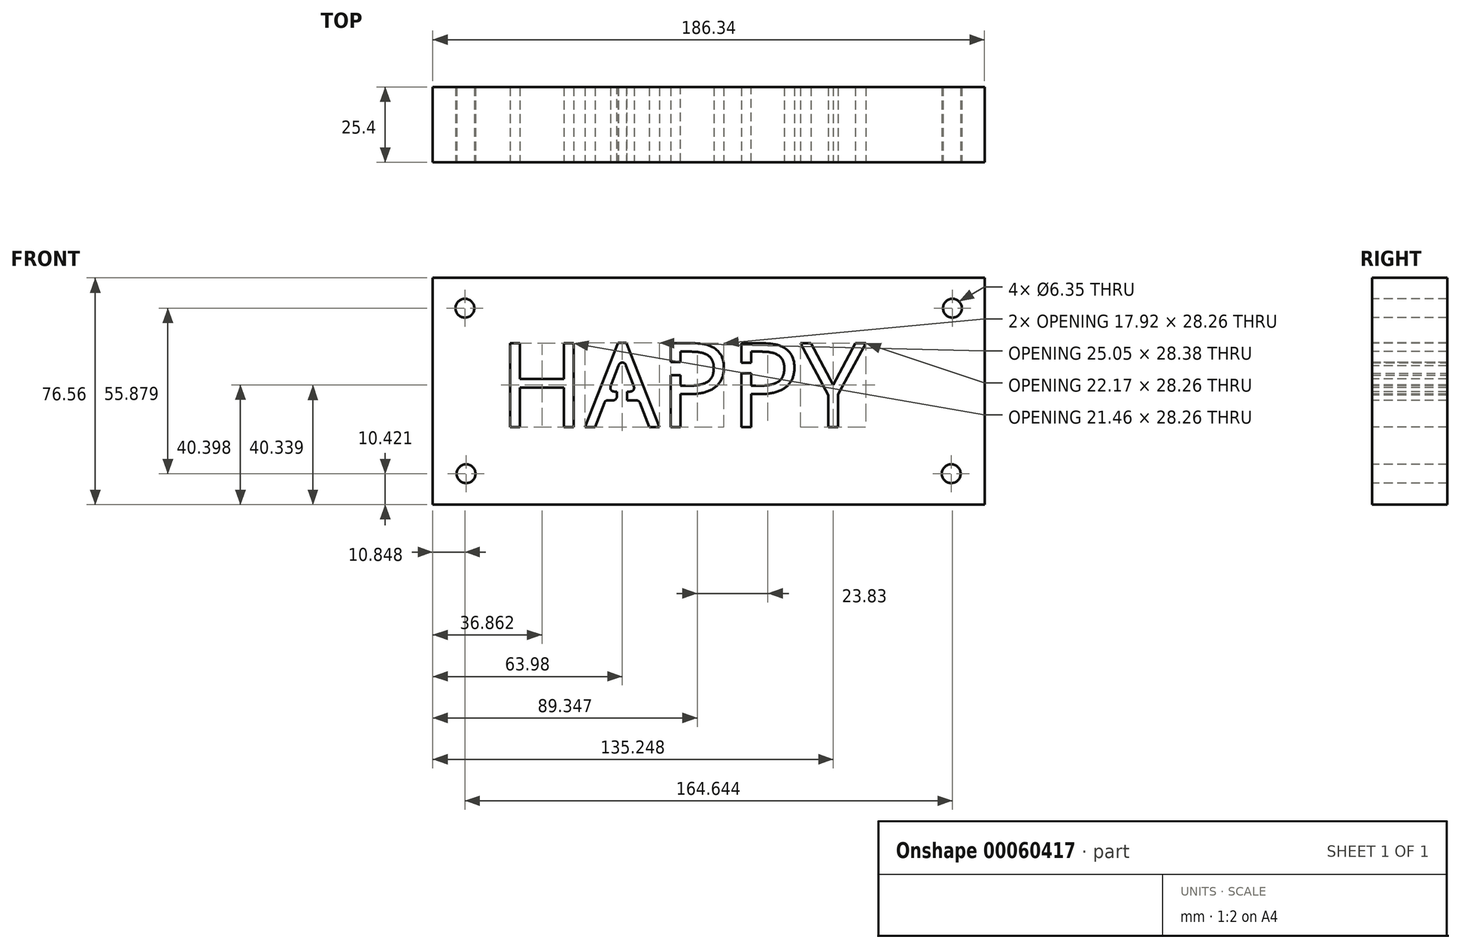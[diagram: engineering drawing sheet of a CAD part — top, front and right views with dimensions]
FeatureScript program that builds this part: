
annotation { "Feature Type Name" : "Feature", "Feature Type Description" : "" }
export const myFeature = defineFeature(function(context is Context, id is Id, definition is map)
    precondition{}
    {
        {
            var Q0;
            Q0=qCreatedBy(makeId("Front.planeOp"),FACE);
            var sketch = newSketch(context, id + "F0", { "sketchPlane" : qUnion([Q0])});
            skLineSegment(sketch, "E0.rect.bottom", {"start": v(93.17, 38.28) * mm, "end": v(-93.17, 38.28) * mm});
            skLineSegment(sketch, "E0.rect.top", {"start": v(93.17, -38.28) * mm, "end": v(-93.17, -38.28) * mm});
            skLineSegment(sketch, "E0.rect.left", {"start": v(93.17, 38.28) * mm, "end": v(93.17, -38.28) * mm});
            skLineSegment(sketch, "E0.rect.right", {"start": v(-93.17, 38.28) * mm, "end": v(-93.17, -38.28) * mm});
            skPoint(sketch, "E0.rect.middle", {"position": v(0, 0) * mm});
            skSolve(sketch);
        }
        {
            var Q0;
            Q0 = qSketchRegion(id + "F0", true);
            extrude(context, id + "F1", {"entities" : qUnion([Q0]), "depth" : 25.4 * mm});
        }
        {
            var Q0;
            Q0=makeQuery(id+"F1.opExtrude","CAP_FACE",FACE,{"disambiguationData":[OSD([sQuery(id+"F0.wireOp",EDGE,"E0.rect.bottom"),sQuery(id+"F0.wireOp",EDGE,"E0.rect.top"),sQuery(id+"F0.wireOp",EDGE,"E0.rect.left"),sQuery(id+"F0.wireOp",EDGE,"E0.rect.right")])],"isStart":false});
            var sketch = newSketch(context, id + "F2", { "sketchPlane" : qUnion([Q0])});
            skText(sketch, "E1", { "text": "HAPPY\n", "fontName": "OpenSans-Regular.ttf"});
            const initialGuessF2  = {"E1": [-0.07092, -0.01207, 1, 0, 0.0285]};
            skSetInitialGuess(sketch, initialGuessF2);
            skSolve(sketch);
        }
        {
            var Q0;
            Q0 = qSketchRegion(id + "F2", true);
            extrude(context, id + "F3", {"entities" : qUnion([Q0]), "operationType" : NewBodyOperationType.REMOVE, "oppositeDirection" : true, "depth" : 0.03 * mm});
        }
        {
            var Q0;
            {var subQ0=sQuery(id+"F0.wireOp",EDGE,"E0.rect.top");var subQ1=sQuery(id+"F0.wireOp",EDGE,"E0.rect.right");var subQ2=sQuery(id+"F0.wireOp",EDGE,"E0.rect.bottom");var subQ3=sQuery(id+"F0.wireOp",EDGE,"E0.rect.left");Q0=makeQuery(id+"F3.boolean.opBoolean","SPLIT",FACE,{"disambiguationData":[TD([makeQuery(id+"F1.opExtrude","SWEPT_FACE",FACE,{"disambiguationData":[OSD([subQ2])]})])],"derivedFrom":makeQuery(id+"F1.opExtrude","CAP_FACE",FACE,{"disambiguationData":[OSD([subQ2,subQ0,subQ3,subQ1])],"isStart":false})});}
            var sketch = newSketch(context, id + "F4", { "sketchPlane" : qUnion([Q0])});
            skLineSegment(sketch, "E2.rect.bottom", {"start": v(-27.48, 0) * mm, "end": v(-31, 0) * mm});
            skLineSegment(sketch, "E2.rect.top", {"start": v(-27.48, -6.16) * mm, "end": v(-31, -6.16) * mm});
            skLineSegment(sketch, "E2.rect.left", {"start": v(-27.48, 0) * mm, "end": v(-27.48, -6.16) * mm});
            skLineSegment(sketch, "E2.rect.right", {"start": v(-31, 0) * mm, "end": v(-31, -6.16) * mm});
            skPoint(sketch, "E2.rect.middle", {"position": v(-29.24, -3.08) * mm});
            skLineSegment(sketch, "E3.rect.bottom", {"start": v(-7.5, 5.36) * mm, "end": v(-18.04, 5.36) * mm});
            skLineSegment(sketch, "E3.rect.top", {"start": v(-7.5, 9.8) * mm, "end": v(-18.04, 9.8) * mm});
            skLineSegment(sketch, "E3.rect.left", {"start": v(-7.5, 5.36) * mm, "end": v(-7.5, 9.8) * mm});
            skLineSegment(sketch, "E3.rect.right", {"start": v(-18.04, 5.36) * mm, "end": v(-18.04, 9.8) * mm});
            skPoint(sketch, "E3.rect.middle", {"position": v(-12.77, 7.58) * mm});
            skLineSegment(sketch, "E4.rect.bottom", {"start": v(16.12, 5.98) * mm, "end": v(6, 5.98) * mm});
            skLineSegment(sketch, "E4.rect.top", {"start": v(16.12, 9.63) * mm, "end": v(6, 9.63) * mm});
            skLineSegment(sketch, "E4.rect.left", {"start": v(16.12, 5.98) * mm, "end": v(16.12, 9.63) * mm});
            skLineSegment(sketch, "E4.rect.right", {"start": v(6, 5.98) * mm, "end": v(6, 9.63) * mm});
            skPoint(sketch, "E4.rect.middle", {"position": v(11.06, 7.8) * mm});
            skSolve(sketch);
        }
        {
            var Q0;
            Q0 = qSketchRegion(id + "F4", true);
            extrude(context, id + "F5", {"entities" : qUnion([Q0]), "operationType" : NewBodyOperationType.ADD, "oppositeDirection" : true, "depth" : 5.08 * mm});
        }
        {
            var Q0;
            Q0=makeQuery(id+"F3.boolean.opBoolean","COPY",FACE,{"derivedFrom":makeQuery(id+"F3.opExtrude","CAP_FACE",FACE,{"disambiguationData":[OSD([sQuery(id+"F2.wireOp",EDGE,"E1.sketch_text.stroke-0"),sQuery(id+"F2.wireOp",EDGE,"E1.sketch_text.stroke-1"),sQuery(id+"F2.wireOp",EDGE,"E1.sketch_text.stroke-2"),sQuery(id+"F2.wireOp",EDGE,"E1.sketch_text.stroke-3"),sQuery(id+"F2.wireOp",EDGE,"E1.sketch_text.stroke-4"),sQuery(id+"F2.wireOp",EDGE,"E1.sketch_text.stroke-5"),sQuery(id+"F2.wireOp",EDGE,"E1.sketch_text.stroke-6"),sQuery(id+"F2.wireOp",EDGE,"E1.sketch_text.stroke-7"),sQuery(id+"F2.wireOp",EDGE,"E1.sketch_text.stroke-8"),sQuery(id+"F2.wireOp",EDGE,"E1.sketch_text.stroke-9"),sQuery(id+"F2.wireOp",EDGE,"E1.sketch_text.stroke-10"),sQuery(id+"F2.wireOp",EDGE,"E1.sketch_text.stroke-11")])],"isStart":false})});
            var Q1;
            Q1=makeQuery(id+"F3.boolean.opBoolean","COPY",FACE,{"derivedFrom":makeQuery(id+"F3.opExtrude","CAP_FACE",FACE,{"disambiguationData":[OSD([sQuery(id+"F2.wireOp",EDGE,"E1.sketch_text.stroke-12"),sQuery(id+"F2.wireOp",EDGE,"E1.sketch_text.stroke-13"),sQuery(id+"F2.wireOp",EDGE,"E1.sketch_text.stroke-14"),sQuery(id+"F2.wireOp",EDGE,"E1.sketch_text.stroke-15"),sQuery(id+"F2.wireOp",EDGE,"E1.sketch_text.stroke-16"),sQuery(id+"F2.wireOp",EDGE,"E1.sketch_text.stroke-17"),sQuery(id+"F2.wireOp",EDGE,"E1.sketch_text.stroke-18"),sQuery(id+"F2.wireOp",EDGE,"E1.sketch_text.stroke-19"),sQuery(id+"F2.wireOp",EDGE,"E1.sketch_text.stroke-20"),sQuery(id+"F2.wireOp",EDGE,"E1.sketch_text.stroke-21"),sQuery(id+"F2.wireOp",EDGE,"E1.sketch_text.stroke-22"),sQuery(id+"F2.wireOp",EDGE,"E1.sketch_text.stroke-23"),sQuery(id+"F2.wireOp",EDGE,"E1.sketch_text.stroke-24")])],"isStart":false})});
            var Q2;
            Q2=makeQuery(id+"F3.boolean.opBoolean","COPY",FACE,{"derivedFrom":makeQuery(id+"F3.opExtrude","CAP_FACE",FACE,{"disambiguationData":[OSD([sQuery(id+"F2.wireOp",EDGE,"E1.sketch_text.stroke-25"),sQuery(id+"F2.wireOp",EDGE,"E1.sketch_text.stroke-26"),sQuery(id+"F2.wireOp",EDGE,"E1.sketch_text.stroke-27"),sQuery(id+"F2.wireOp",EDGE,"E1.sketch_text.stroke-28"),sQuery(id+"F2.wireOp",EDGE,"E1.sketch_text.stroke-29"),sQuery(id+"F2.wireOp",EDGE,"E1.sketch_text.stroke-30"),sQuery(id+"F2.wireOp",EDGE,"E1.sketch_text.stroke-31"),sQuery(id+"F2.wireOp",EDGE,"E1.sketch_text.stroke-32"),sQuery(id+"F2.wireOp",EDGE,"E1.sketch_text.stroke-33"),sQuery(id+"F2.wireOp",EDGE,"E1.sketch_text.stroke-34"),sQuery(id+"F2.wireOp",EDGE,"E1.sketch_text.stroke-35"),sQuery(id+"F2.wireOp",EDGE,"E1.sketch_text.stroke-36"),sQuery(id+"F2.wireOp",EDGE,"E1.sketch_text.stroke-37"),sQuery(id+"F2.wireOp",EDGE,"E1.sketch_text.stroke-38"),sQuery(id+"F2.wireOp",EDGE,"E1.sketch_text.stroke-39")])],"isStart":false})});
            var Q3;
            Q3=makeQuery(id+"F3.boolean.opBoolean","COPY",FACE,{"derivedFrom":makeQuery(id+"F3.opExtrude","CAP_FACE",FACE,{"disambiguationData":[OSD([sQuery(id+"F2.wireOp",EDGE,"E1.sketch_text.stroke-40"),sQuery(id+"F2.wireOp",EDGE,"E1.sketch_text.stroke-41"),sQuery(id+"F2.wireOp",EDGE,"E1.sketch_text.stroke-42"),sQuery(id+"F2.wireOp",EDGE,"E1.sketch_text.stroke-43"),sQuery(id+"F2.wireOp",EDGE,"E1.sketch_text.stroke-44"),sQuery(id+"F2.wireOp",EDGE,"E1.sketch_text.stroke-45"),sQuery(id+"F2.wireOp",EDGE,"E1.sketch_text.stroke-46"),sQuery(id+"F2.wireOp",EDGE,"E1.sketch_text.stroke-47"),sQuery(id+"F2.wireOp",EDGE,"E1.sketch_text.stroke-48"),sQuery(id+"F2.wireOp",EDGE,"E1.sketch_text.stroke-49"),sQuery(id+"F2.wireOp",EDGE,"E1.sketch_text.stroke-50"),sQuery(id+"F2.wireOp",EDGE,"E1.sketch_text.stroke-51"),sQuery(id+"F2.wireOp",EDGE,"E1.sketch_text.stroke-52"),sQuery(id+"F2.wireOp",EDGE,"E1.sketch_text.stroke-53"),sQuery(id+"F2.wireOp",EDGE,"E1.sketch_text.stroke-54")])],"isStart":false})});
            var Q4;
            Q4=makeQuery(id+"F3.boolean.opBoolean","COPY",FACE,{"derivedFrom":makeQuery(id+"F3.opExtrude","CAP_FACE",FACE,{"disambiguationData":[OSD([sQuery(id+"F2.wireOp",EDGE,"E1.sketch_text.stroke-55"),sQuery(id+"F2.wireOp",EDGE,"E1.sketch_text.stroke-56"),sQuery(id+"F2.wireOp",EDGE,"E1.sketch_text.stroke-57"),sQuery(id+"F2.wireOp",EDGE,"E1.sketch_text.stroke-58"),sQuery(id+"F2.wireOp",EDGE,"E1.sketch_text.stroke-59"),sQuery(id+"F2.wireOp",EDGE,"E1.sketch_text.stroke-60"),sQuery(id+"F2.wireOp",EDGE,"E1.sketch_text.stroke-61"),sQuery(id+"F2.wireOp",EDGE,"E1.sketch_text.stroke-62"),sQuery(id+"F2.wireOp",EDGE,"E1.sketch_text.stroke-63")])],"isStart":false})});
            extrude(context, id + "F6", {"entities" : qUnion([Q0, Q1, Q2, Q3, Q4]), "operationType" : NewBodyOperationType.REMOVE, "oppositeDirection" : true, "depth" : 25.4 * mm});
        }
        {
            var Q0;
            {var subQ0=sQuery(id+"F2.wireOp",EDGE,"E1.sketch_text.stroke-22");var subQ1=sQuery(id+"F2.wireOp",EDGE,"E1.sketch_text.stroke-21");Q0=makeQuery(id+"F6.boolean.opBoolean","MERGE",EDGE,{"derivedFrom":[makeQuery(id+"F3.boolean.opBoolean","COPY",EDGE,{"derivedFrom":makeQuery(id+"F3.opExtrude","SWEPT_EDGE",EDGE,{"disambiguationData":[OSD([subQ1,subQ0])]})}),makeQuery(id+"F6.opExtrude","SWEPT_EDGE",EDGE,{"disambiguationData":[OSD([subQ1,subQ0])]})]});}
            var Q1;
            {var subQ0=sQuery(id+"F2.wireOp",EDGE,"E1.sketch_text.stroke-24");var subQ1=sQuery(id+"F2.wireOp",EDGE,"E1.sketch_text.stroke-20");Q1=makeQuery(id+"F6.boolean.opBoolean","MERGE",EDGE,{"derivedFrom":[makeQuery(id+"F3.boolean.opBoolean","COPY",EDGE,{"derivedFrom":makeQuery(id+"F3.opExtrude","SWEPT_EDGE",EDGE,{"disambiguationData":[OSD([subQ1,subQ0])]})}),makeQuery(id+"F6.opExtrude","SWEPT_EDGE",EDGE,{"disambiguationData":[OSD([subQ1,subQ0])]})]});}
            var Q2;
            {var subQ0=sQuery(id+"F2.wireOp",EDGE,"E1.sketch_text.stroke-13");var subQ1=sQuery(id+"F2.wireOp",EDGE,"E1.sketch_text.stroke-12");Q2=makeQuery(id+"F6.boolean.opBoolean","MERGE",EDGE,{"derivedFrom":[makeQuery(id+"F3.boolean.opBoolean","COPY",EDGE,{"derivedFrom":makeQuery(id+"F3.opExtrude","SWEPT_EDGE",EDGE,{"disambiguationData":[OSD([subQ1,subQ0])]})}),makeQuery(id+"F6.opExtrude","SWEPT_EDGE",EDGE,{"disambiguationData":[OSD([subQ1,subQ0])]})]});}
            var Q3;
            {var subQ0=sQuery(id+"F4.wireOp",EDGE,"E2.rect.right");var subQ1=makeQuery(id+"F5.opExtrude","SWEPT_FACE",FACE,{"disambiguationData":[OSD([subQ0])]});var subQ2=sQuery(id+"F2.wireOp",EDGE,"E1.sketch_text.stroke-13");var subQ3=makeQuery(id+"F3.boolean.opBoolean","COPY",FACE,{"derivedFrom":makeQuery(id+"F3.opExtrude","SWEPT_FACE",FACE,{"disambiguationData":[OSD([subQ2])]})});var subQ4=sQuery(id+"F2.wireOp",EDGE,"E1.sketch_text.stroke-24");var subQ5=sQuery(id+"F2.wireOp",EDGE,"E1.sketch_text.stroke-23");var subQ6=sQuery(id+"F2.wireOp",EDGE,"E1.sketch_text.stroke-22");var subQ7=sQuery(id+"F2.wireOp",EDGE,"E1.sketch_text.stroke-21");var subQ8=sQuery(id+"F2.wireOp",EDGE,"E1.sketch_text.stroke-20");var subQ9=sQuery(id+"F2.wireOp",EDGE,"E1.sketch_text.stroke-19");var subQ10=sQuery(id+"F2.wireOp",EDGE,"E1.sketch_text.stroke-18");var subQ11=sQuery(id+"F2.wireOp",EDGE,"E1.sketch_text.stroke-17");var subQ12=sQuery(id+"F2.wireOp",EDGE,"E1.sketch_text.stroke-16");var subQ13=sQuery(id+"F2.wireOp",EDGE,"E1.sketch_text.stroke-15");var subQ14=sQuery(id+"F2.wireOp",EDGE,"E1.sketch_text.stroke-14");var subQ15=sQuery(id+"F2.wireOp",EDGE,"E1.sketch_text.stroke-12");Q3=makeQuery(id+"F6.boolean.opBoolean","MERGE",EDGE,{"derivedFrom":[makeQuery(id+"F5.boolean.opBoolean","INTERSECT",EDGE,{"derivedFrom":[subQ3,subQ1]}),makeQuery(id+"F6.opExtrude","SWEPT_EDGE",EDGE,{"disambiguationData":[OSD([subQ15,subQ2,subQ14,subQ13,subQ12,subQ11,subQ10,subQ9,subQ8,subQ7,subQ6,subQ5,subQ4,subQ0]),TDD([makeQuery(id+"F5.boolean.opBoolean","INTERSECT",VERTEX,{"derivedFrom":[makeQuery(id+"F3.boolean.opBoolean","COPY",FACE,{"derivedFrom":makeQuery(id+"F3.opExtrude","CAP_FACE",FACE,{"disambiguationData":[OSD([subQ15,subQ2,subQ14,subQ13,subQ12,subQ11,subQ10,subQ9,subQ8,subQ7,subQ6,subQ5,subQ4])],"isStart":false})}),subQ3,subQ1]})])]})]});}
            var Q4;
            {var subQ0=sQuery(id+"F2.wireOp",EDGE,"E1.sketch_text.stroke-14");var subQ1=sQuery(id+"F2.wireOp",EDGE,"E1.sketch_text.stroke-13");Q4=makeQuery(id+"F6.boolean.opBoolean","MERGE",EDGE,{"derivedFrom":[makeQuery(id+"F3.boolean.opBoolean","COPY",EDGE,{"derivedFrom":makeQuery(id+"F3.opExtrude","SWEPT_EDGE",EDGE,{"disambiguationData":[OSD([subQ1,subQ0])]})}),makeQuery(id+"F6.opExtrude","SWEPT_EDGE",EDGE,{"disambiguationData":[OSD([subQ1,subQ0])]})]});}
            var Q5;
            {var subQ0=sQuery(id+"F2.wireOp",EDGE,"E1.sketch_text.stroke-24");var subQ1=sQuery(id+"F2.wireOp",EDGE,"E1.sketch_text.stroke-23");Q5=makeQuery(id+"F6.boolean.opBoolean","MERGE",EDGE,{"derivedFrom":[makeQuery(id+"F3.boolean.opBoolean","COPY",EDGE,{"derivedFrom":makeQuery(id+"F3.opExtrude","SWEPT_EDGE",EDGE,{"disambiguationData":[OSD([subQ1,subQ0])]})}),makeQuery(id+"F6.opExtrude","SWEPT_EDGE",EDGE,{"disambiguationData":[OSD([subQ1,subQ0])]})]});}
            fillet(context, id + "F7", {"entities" : qUnion([Q0, Q1, Q2, Q3, Q4, Q5]), "radius" : 1.27 * mm, "tangentPropagation" : true, "allowEdgeOverflow" : false});
        }
        {
            var Q0;
            {var subQ0=sQuery(id+"F0.wireOp",EDGE,"E0.rect.right");var subQ1=sQuery(id+"F0.wireOp",EDGE,"E0.rect.left");var subQ2=sQuery(id+"F0.wireOp",EDGE,"E0.rect.top");var subQ3=sQuery(id+"F0.wireOp",EDGE,"E0.rect.bottom");var subQ4=makeQuery(id+"F1.opExtrude","CAP_FACE",FACE,{"disambiguationData":[OSD([subQ3,subQ2,subQ1,subQ0])],"isStart":false});Q0=makeQuery(id+"F5.boolean.opBoolean","MERGE",FACE,{"derivedFrom":[makeQuery(id+"F3.boolean.opBoolean","SPLIT",FACE,{"disambiguationData":[TD([makeQuery(id+"F1.opExtrude","SWEPT_FACE",FACE,{"disambiguationData":[OSD([subQ3])]})])],"derivedFrom":subQ4}),makeQuery(id+"F3.boolean.opBoolean","SPLIT",FACE,{"disambiguationData":[TD([makeQuery(id+"F3.opExtrude","SWEPT_FACE",FACE,{"disambiguationData":[OSD([sQuery(id+"F2.wireOp",EDGE,"E1.sketch_text.stroke-20")])]})])],"derivedFrom":subQ4}),makeQuery(id+"F3.boolean.opBoolean","SPLIT",FACE,{"disambiguationData":[TD([makeQuery(id+"F3.opExtrude","SWEPT_FACE",FACE,{"disambiguationData":[OSD([sQuery(id+"F2.wireOp",EDGE,"E1.sketch_text.stroke-33")])]})])],"derivedFrom":subQ4}),makeQuery(id+"F3.boolean.opBoolean","SPLIT",FACE,{"disambiguationData":[TD([makeQuery(id+"F3.opExtrude","SWEPT_FACE",FACE,{"disambiguationData":[OSD([sQuery(id+"F2.wireOp",EDGE,"E1.sketch_text.stroke-48")])]})])],"derivedFrom":subQ4}),makeQuery(id+"F5.opExtrude","CAP_FACE",FACE,{"disambiguationData":[OSD([sQuery(id+"F4.wireOp",EDGE,"E2.rect.bottom"),sQuery(id+"F4.wireOp",EDGE,"E2.rect.top"),sQuery(id+"F4.wireOp",EDGE,"E2.rect.left"),sQuery(id+"F4.wireOp",EDGE,"E2.rect.right")])],"isStart":true}),makeQuery(id+"F5.opExtrude","CAP_FACE",FACE,{"disambiguationData":[OSD([sQuery(id+"F4.wireOp",EDGE,"E3.rect.bottom"),sQuery(id+"F4.wireOp",EDGE,"E3.rect.top"),sQuery(id+"F4.wireOp",EDGE,"E3.rect.left"),sQuery(id+"F4.wireOp",EDGE,"E3.rect.right")])],"isStart":true}),makeQuery(id+"F5.opExtrude","CAP_FACE",FACE,{"disambiguationData":[OSD([sQuery(id+"F4.wireOp",EDGE,"E4.rect.bottom"),sQuery(id+"F4.wireOp",EDGE,"E4.rect.top"),sQuery(id+"F4.wireOp",EDGE,"E4.rect.left"),sQuery(id+"F4.wireOp",EDGE,"E4.rect.right")])],"isStart":true})]});}
            var sketch = newSketch(context, id + "F8", { "sketchPlane" : qUnion([Q0])});
            skCircle(sketch, "E5", {"center": v(-81.92, -27.86) * mm, "radius": 3.18 * mm});
            skLineSegment(sketch, "E6", {"start": v(-93.17, 0) * mm, "end": v(93.17, 1.36) * mm, "construction": true});
            skLineSegment(sketch, "E7", {"start": v(0, -38.28) * mm, "end": v(0, 38.28) * mm, "construction": true});
            skCircle(sketch, "E8.MirrorC", {"center": v(-82.32, 28.02) * mm, "radius": 3.18 * mm});
            skCircle(sketch, "E9.MirrorC", {"center": v(81.92, -27.86) * mm, "radius": 3.18 * mm});
            skCircle(sketch, "E10.MirrorC", {"center": v(82.32, 28.02) * mm, "radius": 3.18 * mm});
            skSolve(sketch);
        }
        {
            var Q0;
            Q0 = qSketchRegion(id + "F8", true);
            extrude(context, id + "F9", {"entities" : qUnion([Q0]), "operationType" : NewBodyOperationType.REMOVE, "oppositeDirection" : true, "depth" : 25.4 * mm});
        }
    });
